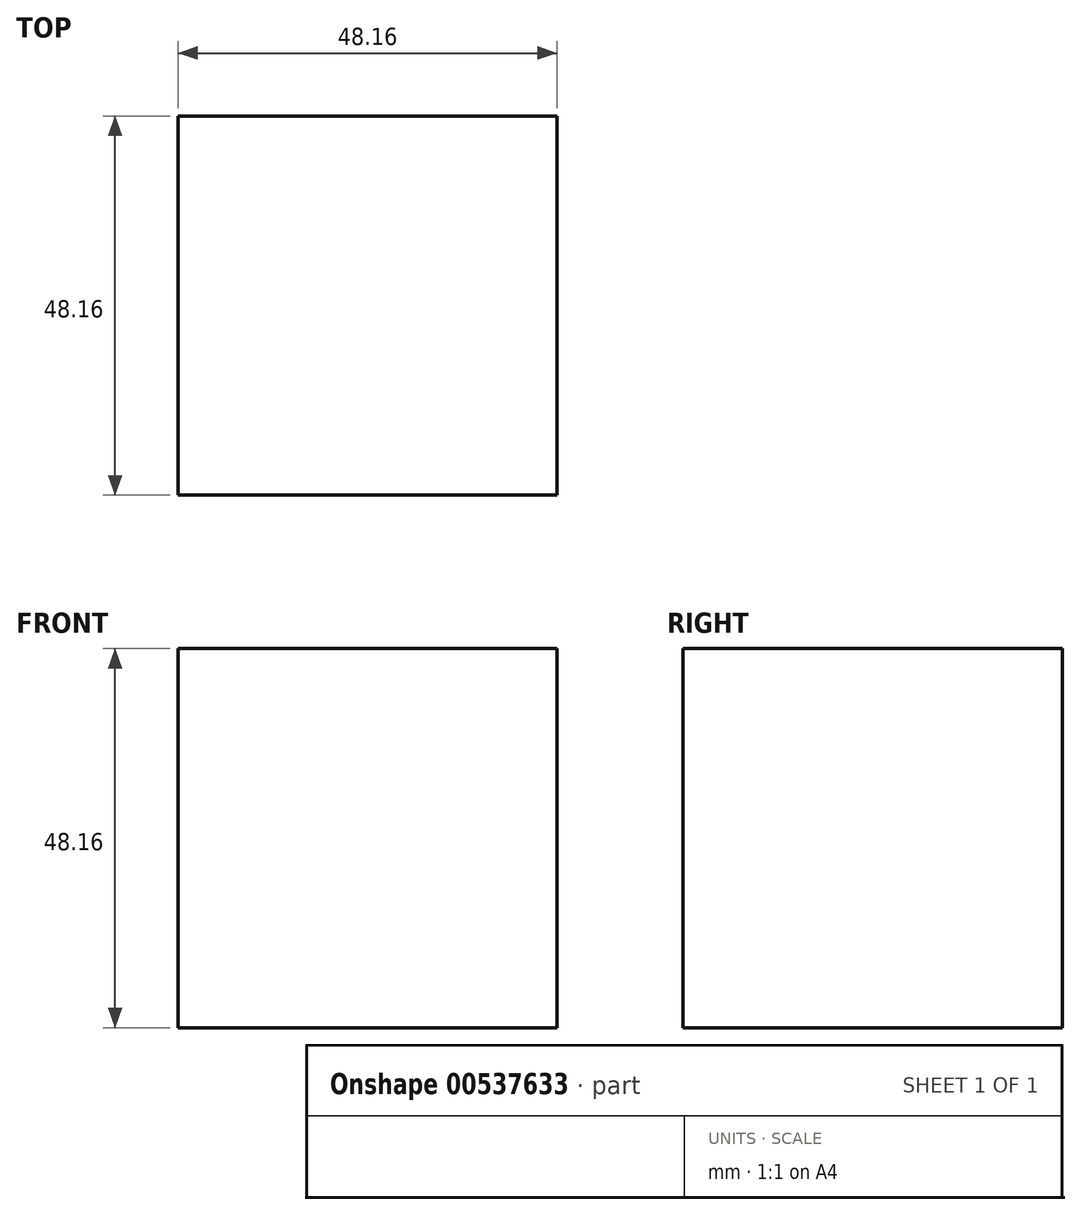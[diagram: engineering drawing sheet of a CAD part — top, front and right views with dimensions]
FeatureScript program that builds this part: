
annotation { "Feature Type Name" : "Feature", "Feature Type Description" : "" }
export const myFeature = defineFeature(function(context is Context, id is Id, definition is map)
    precondition{}
    {
        {
            var Q0;
            Q0=qCreatedBy(makeId("Top.planeOp"),FACE);
            var sketch = newSketch(context, id + "F0", { "sketchPlane" : qUnion([Q0])});
            skLineSegment(sketch, "E0.bottom", {"start": v(-24.08, 24.08) * mm, "end": v(24.08, 24.08) * mm});
            skLineSegment(sketch, "E0.top", {"start": v(-24.08, -24.08) * mm, "end": v(24.08, -24.08) * mm});
            skLineSegment(sketch, "E0.left", {"start": v(-24.08, 24.08) * mm, "end": v(-24.08, -24.08) * mm});
            skLineSegment(sketch, "E0.right", {"start": v(24.08, 24.08) * mm, "end": v(24.08, -24.08) * mm});
            skPoint(sketch, "E0.middle", {"position": v(0, 0) * mm});
            skSolve(sketch);
        }
        {
            var Q0;
            Q0=makeQuery(id+"F0.imprint","IMPRINT",FACE,{"disambiguationData":[TD([[makeQuery(id+"F0.imprint","IMPRINT",EDGE,{"derivedFrom":sQuery(id+"F0.wireOp",EDGE,"E0.bottom")}),-1.0]])]});
            extrude(context, id + "F1", {"entities" : qUnion([Q0]), "depth" : 48.16 * mm, "offsetDistance" : 25.4 * mm});
        }
    });
